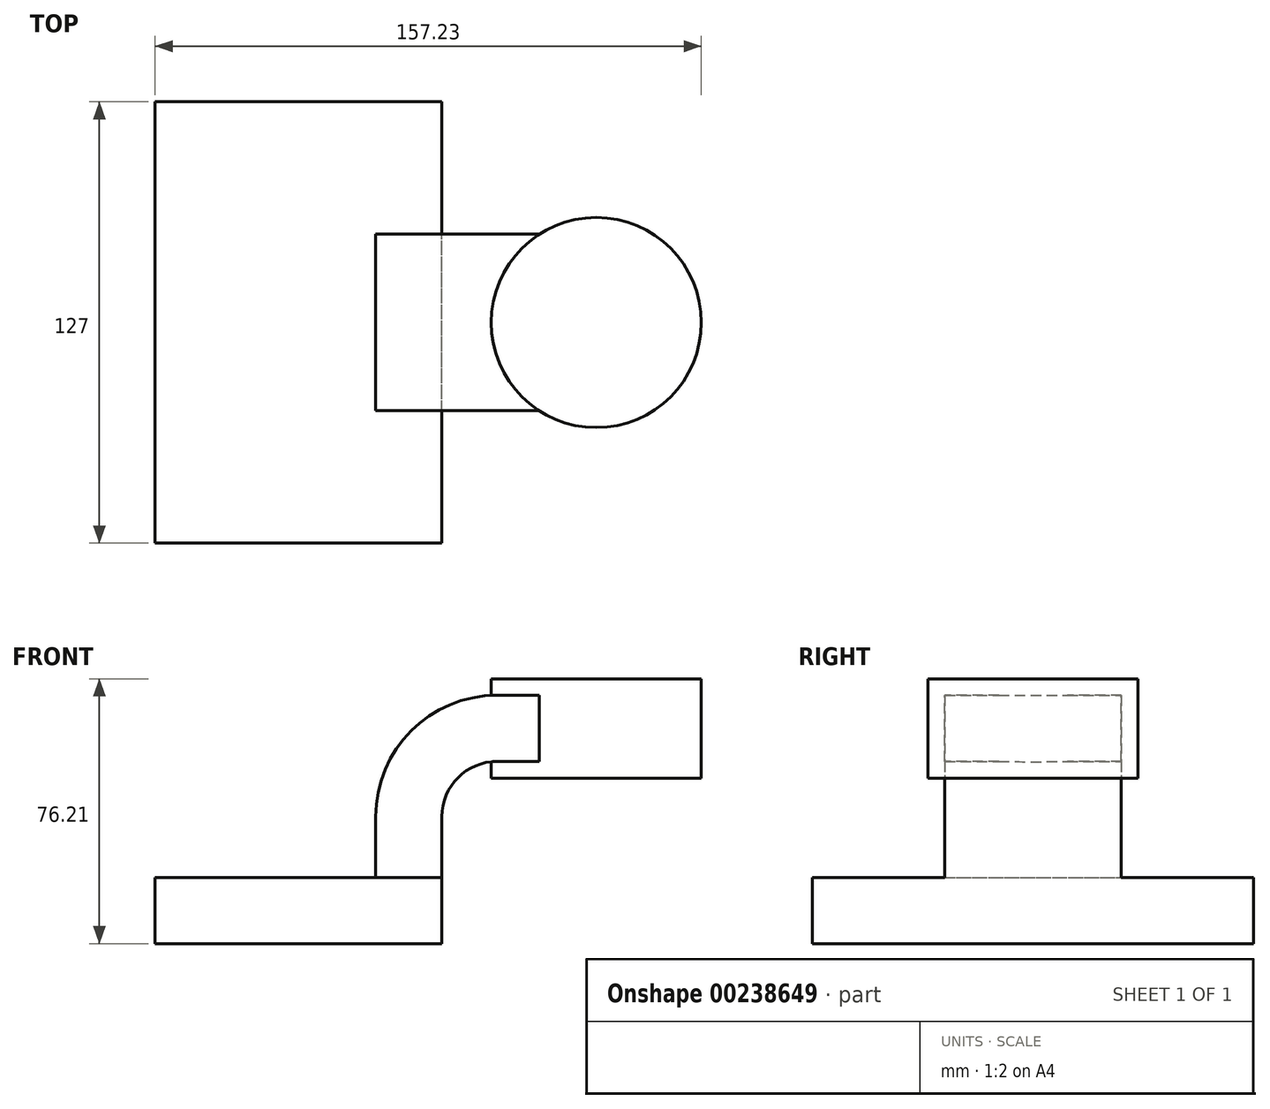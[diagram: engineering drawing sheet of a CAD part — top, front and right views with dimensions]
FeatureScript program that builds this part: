
annotation { "Feature Type Name" : "Feature", "Feature Type Description" : "" }
export const myFeature = defineFeature(function(context is Context, id is Id, definition is map)
    precondition{}
    {
        {
            var Q0;
            Q0=qCreatedBy(makeId("Front.planeOp"),FACE);
            var sketch = newSketch(context, id + "F0", { "sketchPlane" : qUnion([Q0])});
            skLineSegment(sketch, "E0.bottom", {"start": v(-41.28, 9.52) * mm, "end": v(41.27, 9.53) * mm});
            skLineSegment(sketch, "E0.top", {"start": v(-41.28, -9.53) * mm, "end": v(41.28, -9.53) * mm});
            skLineSegment(sketch, "E0.left", {"start": v(-41.28, 9.52) * mm, "end": v(-41.27, -9.53) * mm});
            skLineSegment(sketch, "E0.right", {"start": v(41.28, 9.53) * mm, "end": v(41.28, -9.52) * mm});
            skPoint(sketch, "E0.middle", {"position": v(0, 0) * mm});
            skLineSegment(sketch, "E1.bottom", {"start": v(65.16, 66.67) * mm, "end": v(115.96, 66.67) * mm});
            skLineSegment(sketch, "E1.top", {"start": v(65.16, 38.1) * mm, "end": v(115.96, 38.1) * mm});
            skLineSegment(sketch, "E1.left", {"start": v(65.16, 66.67) * mm, "end": v(65.16, 38.1) * mm});
            skLineSegment(sketch, "E1.right", {"start": v(115.96, 66.67) * mm, "end": v(115.96, 38.1) * mm});
            skPoint(sketch, "E1.middle", {"position": v(90.56, 52.39) * mm});
            skLineSegment(sketch, "E2", {"start": v(41.27, 9.53) * mm, "end": v(41.27, 27) * mm});
            skArc(sketch, "E3", {"start": v(41.27, 27) * mm, "mid": v(45.92, 38.23) * mm, "end": v(57.15, 42.88) * mm});
            skLineSegment(sketch, "E4", {"start": v(57.15, 42.88) * mm, "end": v(85.73, 42.88) * mm});
            skLineSegment(sketch, "E5.0", {"start": v(57.15, 61.93) * mm, "end": v(85.73, 61.93) * mm});
            skArc(sketch, "E5.1", {"start": v(22.23, 27) * mm, "mid": v(32.45, 51.7) * mm, "end": v(57.15, 61.93) * mm});
            skLineSegment(sketch, "E5.2", {"start": v(22.23, 9.53) * mm, "end": v(22.23, 27) * mm});
            skLineSegment(sketch, "E6", {"start": v(85.73, 61.93) * mm, "end": v(85.73, 42.88) * mm});
            skFitSpline(sketch, "E7", {"points": [v(65.16, 66.67) * mm, v(-41.28, 9.52) * mm], "startDerivative": vector(-154.72, 1.53) * mm, "endDerivative": vector(-3.04, -110.4) * mm});
            skLineSegment(sketch, "E8", {"start": v(85.73, 42.88) * mm, "end": v(85.73, 38.1) * mm});
            skPoint(sketch, "E8.endSnap0", {"position": v(90.56, 38.1) * mm});
            skLineSegment(sketch, "E9", {"start": v(85.73, 61.93) * mm, "end": v(85.73, 66.67) * mm});
            skSolve(sketch);
        }
        {
            var Q0;
            Q0=makeQuery(id+"F0.imprint","IMPRINT",FACE,{"disambiguationData":[TD([[makeQuery(id+"F0.imprint","IMPRINT",EDGE,{"derivedFrom":sQuery(id+"F0.wireOp",EDGE,"E0.top")}),1.0]])]});
            extrude(context, id + "F1", {"entities" : qUnion([Q0]), "endBound" : BoundingType.SYMMETRIC, "depth" : 127 * mm});
        }
        {
            var Q0;
            {var subQ1=sQuery(id+"F0.wireOp",EDGE,"E2");Q0=makeQuery(id+"F0.imprint","IMPRINT",FACE,{"disambiguationData":[TD([[makeQuery(id+"F0.imprint","IMPRINT",EDGE,{"derivedFrom":subQ1}),1.0]])]});}
            var Q1;
            {var subQ5=sQuery(id+"F0.wireOp",EDGE,"E6");Q1=makeQuery(id+"F0.imprint","IMPRINT",FACE,{"disambiguationData":[TD([[makeQuery(id+"F0.imprint","IMPRINT",EDGE,{"derivedFrom":subQ5}),-1.0]])]});}
            extrude(context, id + "F2", {"entities" : qUnion([Q0, Q1]), "operationType" : NewBodyOperationType.ADD, "endBound" : BoundingType.SYMMETRIC, "depth" : 50.8 * mm});
        }
        {
            var Q0;
            {var subQ0=sQuery(id+"F0.wireOp",EDGE,"E5.1");Q0=makeQuery(id+"F0.imprint","IMPRINT",FACE,{"disambiguationData":[TD([[makeQuery(id+"F0.imprint","IMPRINT",EDGE,{"derivedFrom":subQ0}),1.0]])]});}
            extrude(context, id + "F3", {"entities" : qUnion([Q0]), "operationType" : NewBodyOperationType.ADD, "endBound" : BoundingType.SYMMETRIC, "depth" : 15.88 * mm});
        }
        {
            var Q0;
            {var subQ0=sQuery(id+"F0.wireOp",EDGE,"E1.right");Q0=makeQuery(id+"F0.imprint","IMPRINT",FACE,{"disambiguationData":[TD([[makeQuery(id+"F0.imprint","IMPRINT",EDGE,{"derivedFrom":subQ0}),-1.0]])]});}
            var Q1;
            Q1=sQuery(id+"F0.wireOp",EDGE,"E8");
            revolve(context, id + "F4", {"operationType" : NewBodyOperationType.ADD, "entities" : qUnion([Q0]), "axis" : qUnion([Q1]), "revolveType" : RevolveType.FULL});
        }
    });
